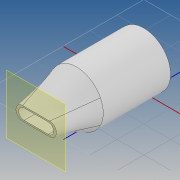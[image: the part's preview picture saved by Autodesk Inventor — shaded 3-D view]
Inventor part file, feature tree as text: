
AUTODESK INVENTOR PART (.ipt)
format: ipt  version: 2021 (Build 250183000, 183)  size: 156,672 bytes
history: native  units: mm
features: sketch x4, extrude x3, plane x1, loft x1, projected_geometry x1, other x1
ambient origin geometry x8: Origin, YZ Plane, XZ Plane, XY Plane, X Axis, Y Axis, Z Axis, Center Point
bodies: Solid1 (feature_tree)
feature tree (11):
  extrude  "Extrusion1"  Depth=30.0mm
  plane  "Work Plane1"
  loft  "Loft1"
  extrude  "Extrusion2"  TaperAngle=0.0deg  [1 undecoded]
  extrude  "Extrusion3"  Depth=50.0mm TaperAngle=0.0deg
  sketch  "Sketch2"  dims[d2=50.0mm d3=0.0mm d4=30.0mm]
  sketch  "Sketch3"  dims[d5=10.0mm d6=10.0mm]
  projected_geometry  "Projected Loop1"
  other  "Edges1"
  sketch  "Sketch4"  dims[d7=0.0mm d8=90.0deg d9=0.0mm d10=90.0deg]
  sketch  "Sketch5"  dims[d11=34.65mm d12=50.0mm d13=0.0mm d14=9.0mm d15=180.0deg d16=8.0mm d17=30.0mm d18=0.0mm]
note: 1 required parameter value undecoded (feature->parameter linkage not recoverable at this tier; creation-order binding heuristic only, values carry confidence <= 0.55)
